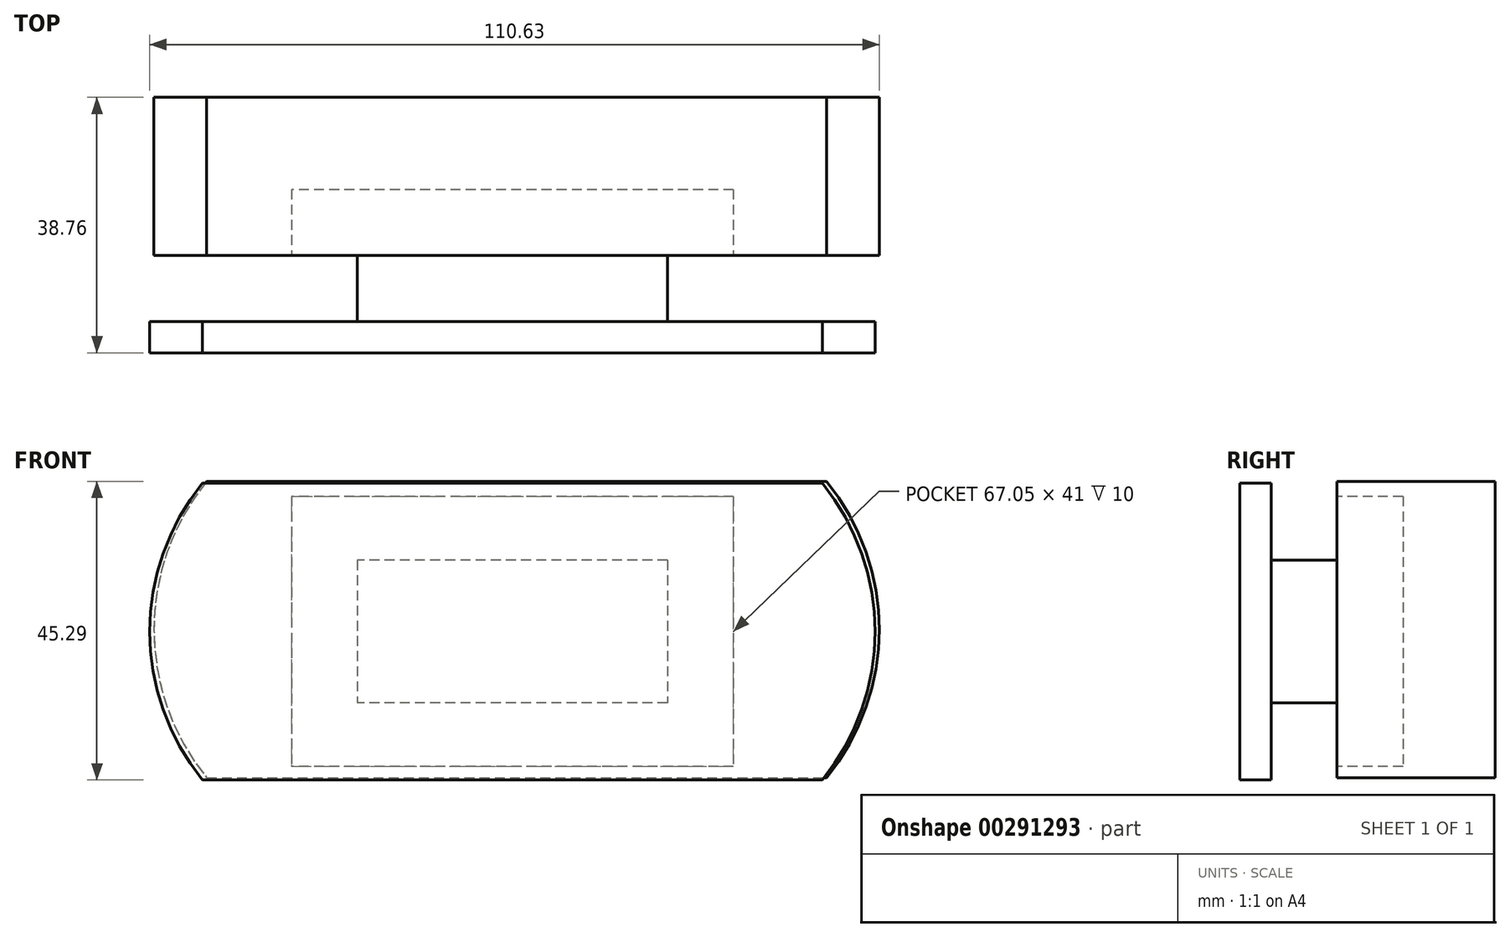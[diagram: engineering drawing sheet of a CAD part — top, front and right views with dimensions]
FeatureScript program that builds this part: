
annotation { "Feature Type Name" : "Feature", "Feature Type Description" : "" }
export const myFeature = defineFeature(function(context is Context, id is Id, definition is map)
    precondition{}
    {
        {
            var Q0;
            Q0=qCreatedBy(makeId("Front.planeOp"),FACE);
            var sketch = newSketch(context, id + "F0", { "sketchPlane" : qUnion([Q0])});
            skLineSegment(sketch, "E0.bottom", {"start": v(23.52, 10.83) * mm, "end": v(-23.53, 10.82) * mm});
            skLineSegment(sketch, "E0.top", {"start": v(23.53, -10.82) * mm, "end": v(-23.52, -10.83) * mm});
            skLineSegment(sketch, "E0.left", {"start": v(23.52, 10.83) * mm, "end": v(23.53, -10.82) * mm});
            skLineSegment(sketch, "E0.right", {"start": v(-23.53, 10.82) * mm, "end": v(-23.52, -10.83) * mm});
            skPoint(sketch, "E0.middle", {"position": v(0, 0) * mm});
            skSolve(sketch);
        }
        {
            var Q0;
            Q0=makeQuery(id+"F0.imprint","IMPRINT",FACE,{"disambiguationData":[TD([[makeQuery(id+"F0.imprint","IMPRINT",EDGE,{"derivedFrom":sQuery(id+"F0.wireOp",EDGE,"E0.bottom")}),1.0]])]});
            extrude(context, id + "F1", {"entities" : qUnion([Q0]), "endBound" : BoundingType.SYMMETRIC, "depth" : 10 * mm});
        }
        {
            var Q0;
            Q0=makeQuery(id+"F1.opExtrude","CAP_FACE",FACE,{"disambiguationData":[OSD([sQuery(id+"F0.wireOp",EDGE,"E0.bottom"),sQuery(id+"F0.wireOp",EDGE,"E0.top"),sQuery(id+"F0.wireOp",EDGE,"E0.left"),sQuery(id+"F0.wireOp",EDGE,"E0.right")])],"isStart":false});
            var sketch = newSketch(context, id + "F2", { "sketchPlane" : qUnion([Q0])});
            skPoint(sketch, "E1.middle", {"position": v(0, 0) * mm});
            skLineSegment(sketch, "E2.bottom", {"start": v(47, 22.5) * mm, "end": v(-47, 22.5) * mm});
            skLineSegment(sketch, "E2.top", {"start": v(47, -22.5) * mm, "end": v(-47, -22.5) * mm});
            skLineSegment(sketch, "E2.left", {"start": v(47, 22.5) * mm, "end": v(47, -22.5) * mm});
            skLineSegment(sketch, "E2.right", {"start": v(-47, 22.5) * mm, "end": v(-47, -22.5) * mm});
            skPoint(sketch, "E3", {"position": v(-55, 0) * mm});
            skPoint(sketch, "E4", {"position": v(55, 0) * mm});
            skArc(sketch, "E5", {"start": v(-47, 22.5) * mm, "mid": v(-55, 0) * mm, "end": v(-47, -22.5) * mm});
            skArc(sketch, "E6", {"start": v(47, -22.5) * mm, "mid": v(55, 0) * mm, "end": v(47, 22.5) * mm});
            skPoint(sketch, "E7", {"position": v(47, 22.5) * mm});
            skPoint(sketch, "E8", {"position": v(47, -22.5) * mm});
            skPoint(sketch, "E9", {"position": v(-47, -22.5) * mm});
            skPoint(sketch, "E10", {"position": v(-47, 22.5) * mm});
            skLineSegment(sketch, "E11", {"start": v(-47, 22.5) * mm, "end": v(47, 22.5) * mm});
            skLineSegment(sketch, "E12", {"start": v(-47, -22.5) * mm, "end": v(47, -22.5) * mm});
            skLineSegment(sketch, "E13.bottom", {"start": v(42.5, 22.5) * mm, "end": v(-42.5, 22.5) * mm});
            skLineSegment(sketch, "E13.top", {"start": v(42.5, -22.5) * mm, "end": v(-42.5, -22.5) * mm});
            skLineSegment(sketch, "E13.left", {"start": v(42.5, 22.5) * mm, "end": v(42.5, -22.5) * mm});
            skLineSegment(sketch, "E13.right", {"start": v(-42.5, 22.5) * mm, "end": v(-42.5, -22.5) * mm});
            skSolve(sketch);
        }
        {
            var Q0;
            Q0 = qSketchRegion(id + "F2", true);
            extrude(context, id + "F3", {"entities" : qUnion([Q0]), "operationType" : NewBodyOperationType.ADD, "depth" : 4.76 * mm});
        }
        {
            var Q0;
            Q0=makeQuery(id+"F1.opExtrude","CAP_FACE",FACE,{"disambiguationData":[OSD([sQuery(id+"F0.wireOp",EDGE,"E0.bottom"),sQuery(id+"F0.wireOp",EDGE,"E0.top"),sQuery(id+"F0.wireOp",EDGE,"E0.left"),sQuery(id+"F0.wireOp",EDGE,"E0.right")])],"isStart":true});
            var sketch = newSketch(context, id + "F4", { "sketchPlane" : qUnion([Q0])});
            skLineSegment(sketch, "E14.top", {"start": v(46.37, -22.2) * mm, "end": v(-47.63, -22.2) * mm});
            skLineSegment(sketch, "E14.left", {"start": v(46.37, 22.8) * mm, "end": v(46.37, -22.2) * mm});
            skLineSegment(sketch, "E14.right", {"start": v(-47.63, 22.8) * mm, "end": v(-47.63, -22.2) * mm});
            skArc(sketch, "E15", {"start": v(-47.63, 22.8) * mm, "mid": v(-55.63, 0.3) * mm, "end": v(-47.63, -22.2) * mm});
            skArc(sketch, "E16", {"start": v(46.37, -22.2) * mm, "mid": v(54.37, 0.3) * mm, "end": v(46.37, 22.8) * mm});
            skLineSegment(sketch, "E17", {"start": v(-47.63, 22.8) * mm, "end": v(46.37, 22.8) * mm});
            skLineSegment(sketch, "E18.left", {"start": v(41.87, 22.8) * mm, "end": v(41.87, -22.2) * mm});
            skLineSegment(sketch, "E18.right", {"start": v(-43.13, 22.8) * mm, "end": v(-43.13, -22.2) * mm});
            skSolve(sketch);
        }
        {
            var Q0;
            Q0 = qSketchRegion(id + "F4", true);
            var Q1;
            Q1 = qConstructionFilter(qBodyType(qCreatedBy(id + "F4" ,EDGE), BodyType.WIRE), ConstructionObject.NO);
            extrude(context, id + "F5", {"entities" : qUnion([Q0]), "surfaceEntities" : qUnion([Q1]), "depth" : 24 * mm});
        }
        {
            var Q0;
            Q0=makeQuery(id+"F5.opExtrude","CAP_FACE",FACE,{"disambiguationData":[OSD([sQuery(id+"F4.wireOp",EDGE,"E14.top"),sQuery(id+"F4.wireOp",EDGE,"E15"),sQuery(id+"F4.wireOp",EDGE,"E16"),sQuery(id+"F4.wireOp",EDGE,"E17")])],"isStart":true});
            var sketch = newSketch(context, id + "F6", { "sketchPlane" : qUnion([Q0])});
            skLineSegment(sketch, "E19.bottom", {"start": v(33.52, 20.5) * mm, "end": v(-33.52, 20.5) * mm});
            skLineSegment(sketch, "E19.top", {"start": v(33.52, -20.5) * mm, "end": v(-33.52, -20.5) * mm});
            skLineSegment(sketch, "E19.left", {"start": v(33.52, 20.5) * mm, "end": v(33.52, -20.5) * mm});
            skLineSegment(sketch, "E19.right", {"start": v(-33.52, 20.5) * mm, "end": v(-33.52, -20.5) * mm});
            skPoint(sketch, "E19.middle", {"position": v(0, 0) * mm});
            skSolve(sketch);
        }
        {
            var Q0;
            Q0=makeQuery(id+"F6.imprint","IMPRINT",FACE,{"disambiguationData":[TD([[makeQuery(id+"F6.imprint","IMPRINT",EDGE,{"derivedFrom":sQuery(id+"F6.wireOp",EDGE,"E19.bottom")}),1.0]])]});
            extrude(context, id + "F7", {"entities" : qUnion([Q0]), "operationType" : NewBodyOperationType.REMOVE, "oppositeDirection" : true, "depth" : 10 * mm});
        }
    });
